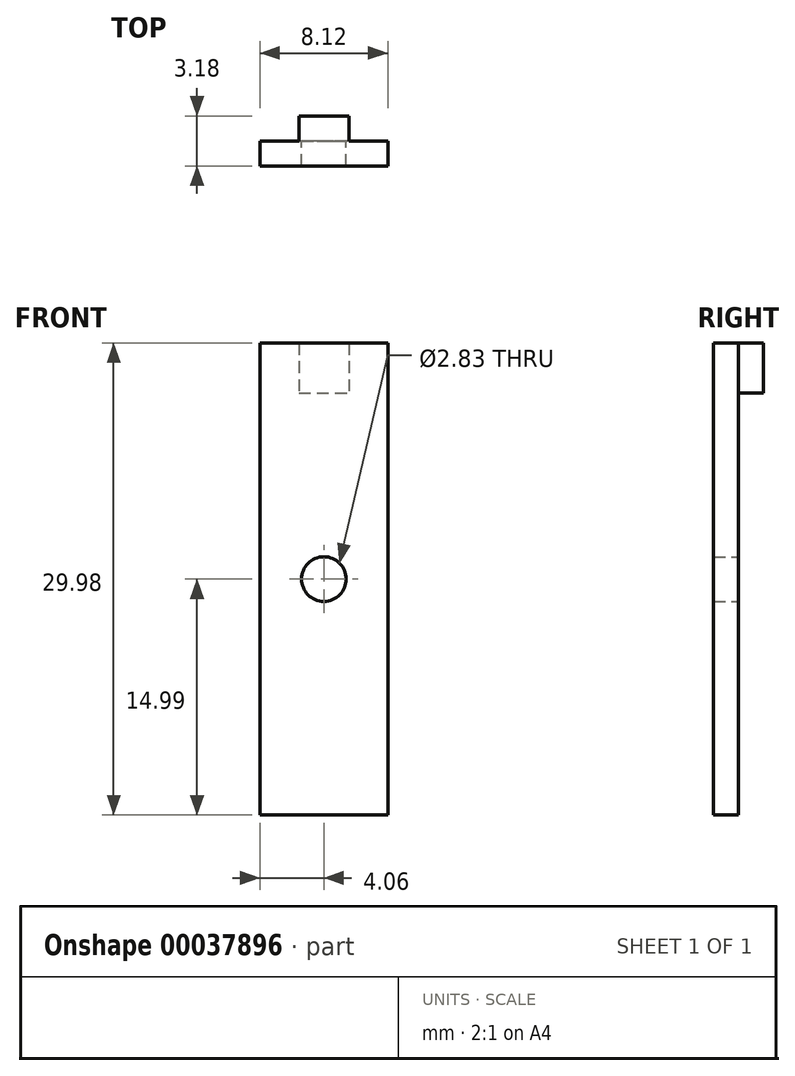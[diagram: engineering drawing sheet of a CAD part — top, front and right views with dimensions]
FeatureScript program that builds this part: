
annotation { "Feature Type Name" : "Feature", "Feature Type Description" : "" }
export const myFeature = defineFeature(function(context is Context, id is Id, definition is map)
    precondition{}
    {
        {
            var Q0;
            Q0=qCreatedBy(makeId("Front.planeOp"),FACE);
            var sketch = newSketch(context, id + "F0", { "sketchPlane" : qUnion([Q0])});
            skCircle(sketch, "E0", {"center": v(0, 0) * mm, "radius": 1.42 * mm});
            skLineSegment(sketch, "E1.rect.bottom", {"start": v(4.06, 14.99) * mm, "end": v(-4.06, 14.99) * mm});
            skLineSegment(sketch, "E1.rect.top", {"start": v(4.06, -14.99) * mm, "end": v(-4.06, -14.99) * mm});
            skLineSegment(sketch, "E1.rect.left", {"start": v(4.06, 14.99) * mm, "end": v(4.06, -14.99) * mm});
            skLineSegment(sketch, "E1.rect.right", {"start": v(-4.06, 14.99) * mm, "end": v(-4.06, -14.99) * mm});
            skSolve(sketch);
        }
        {
            var Q0;
            Q0 = qSketchRegion(id + "F0", true);
            extrude(context, id + "F1", {"entities" : qUnion([Q0]), "depth" : 1.59 * mm});
        }
        {
            var Q0;
            Q0=makeQuery(id+"F1.opExtrude","CAP_FACE",FACE,{"disambiguationData":[OSD([sQuery(id+"F0.wireOp",EDGE,"E0"),sQuery(id+"F0.wireOp",EDGE,"E1.rect.bottom"),sQuery(id+"F0.wireOp",EDGE,"E1.rect.top"),sQuery(id+"F0.wireOp",EDGE,"E1.rect.left"),sQuery(id+"F0.wireOp",EDGE,"E1.rect.right")])],"isStart":true});
            var sketch = newSketch(context, id + "F2", { "sketchPlane" : qUnion([Q0])});
            skLineSegment(sketch, "E2.bottom", {"start": v(1.59, 14.99) * mm, "end": v(-1.59, 14.99) * mm});
            skLineSegment(sketch, "E2.top", {"start": v(1.59, 11.81) * mm, "end": v(-1.59, 11.81) * mm});
            skLineSegment(sketch, "E2.left", {"start": v(1.59, 14.99) * mm, "end": v(1.59, 11.81) * mm});
            skLineSegment(sketch, "E2.right", {"start": v(-1.59, 14.99) * mm, "end": v(-1.59, 11.81) * mm});
            skPoint(sketch, "E3", {"position": v(0, 14.99) * mm});
            skSolve(sketch);
        }
        {
            var Q0;
            Q0 = qSketchRegion(id + "F2", true);
            extrude(context, id + "F3", {"entities" : qUnion([Q0]), "operationType" : NewBodyOperationType.ADD, "depth" : 1.59 * mm});
        }
    });
